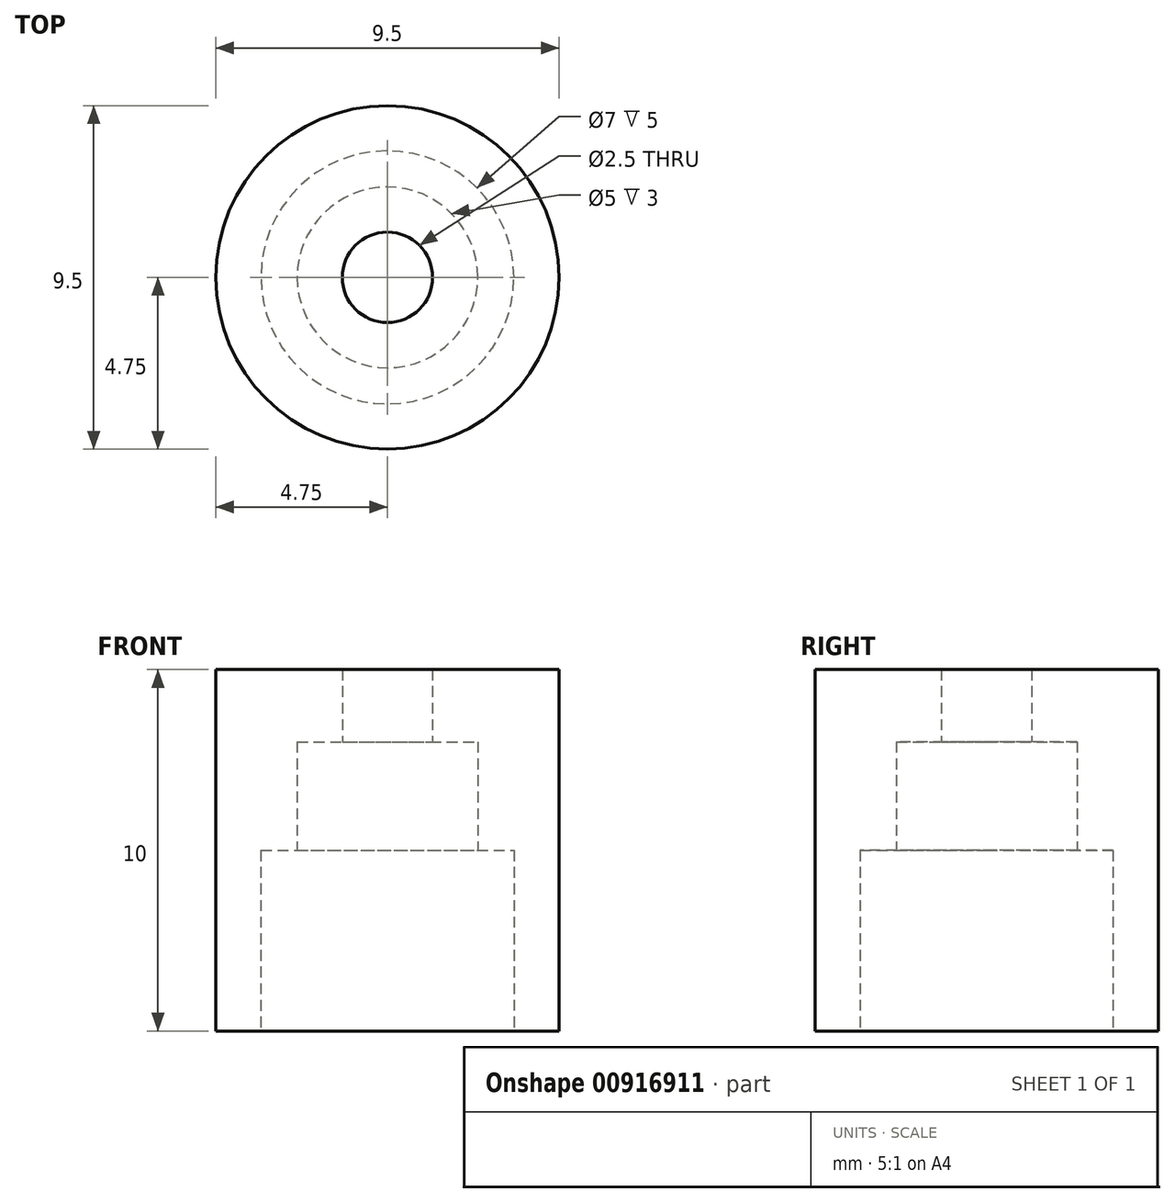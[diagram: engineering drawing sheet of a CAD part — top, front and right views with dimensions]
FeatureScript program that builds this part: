
annotation { "Feature Type Name" : "Feature", "Feature Type Description" : "" }
export const myFeature = defineFeature(function(context is Context, id is Id, definition is map)
    precondition{}
    {
        {
            var Q0;
            Q0=qCreatedBy(makeId("Front.planeOp"),FACE);
            var sketch = newSketch(context, id + "F0", { "sketchPlane" : qUnion([Q0])});
            skLineSegment(sketch, "E0", {"start": v(0, 0) * mm, "end": v(0, 10.68) * mm, "construction": true});
            skLineSegment(sketch, "E1", {"start": v(3.5, 0) * mm, "end": v(4.75, 0) * mm});
            skLineSegment(sketch, "E2", {"start": v(4.75, 0) * mm, "end": v(4.75, 10) * mm});
            skLineSegment(sketch, "E3", {"start": v(4.75, 10) * mm, "end": v(1.25, 10) * mm});
            skLineSegment(sketch, "E4", {"start": v(1.25, 10) * mm, "end": v(1.25, 8) * mm});
            skLineSegment(sketch, "E5", {"start": v(1.25, 8) * mm, "end": v(2.5, 8) * mm});
            skLineSegment(sketch, "E6", {"start": v(3.5, 5) * mm, "end": v(3.5, 0) * mm});
            skLineSegment(sketch, "E7", {"start": v(2.5, 8) * mm, "end": v(2.5, 5) * mm});
            skLineSegment(sketch, "E8", {"start": v(2.5, 5) * mm, "end": v(3.5, 5) * mm});
            skSolve(sketch);
        }
        {
            var Q0;
            Q0 = qSketchRegion(id + "F0", true);
            var Q1;
            Q1=sQuery(id+"F0.wireOp",EDGE,"E0");
            revolve(context, id + "F1", {"surfaceOperationType" : NewSurfaceOperationType.NEW, "entities" : qUnion([Q0]), "axis" : qUnion([Q1]), "revolveType" : RevolveType.FULL});
        }
    });
